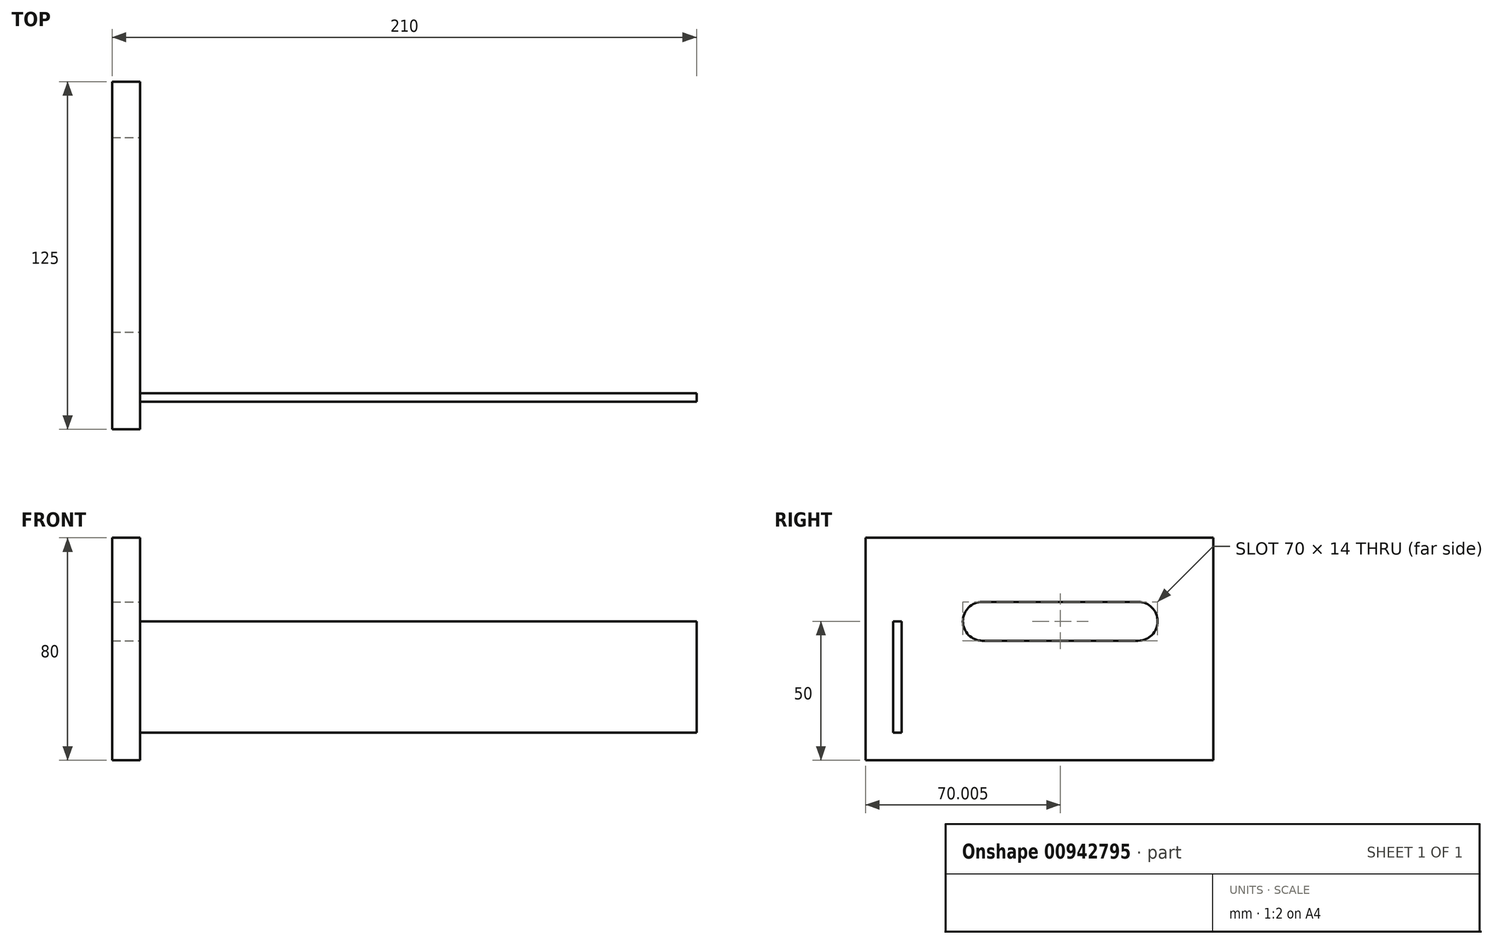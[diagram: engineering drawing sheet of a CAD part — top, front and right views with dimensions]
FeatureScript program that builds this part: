
annotation { "Feature Type Name" : "Feature", "Feature Type Description" : "" }
export const myFeature = defineFeature(function(context is Context, id is Id, definition is map)
    precondition{}
    {
        {
            var Q0;
            Q0=qCreatedBy(makeId("Top.planeOp"),FACE);
            var sketch = newSketch(context, id + "F0", { "sketchPlane" : qUnion([Q0])});
            skLineSegment(sketch, "E0.bottom", {"start": v(-39.22, -18.45) * mm, "end": v(-29.22, -18.45) * mm});
            skLineSegment(sketch, "E0.top", {"start": v(-39.22, 106.55) * mm, "end": v(-29.22, 106.55) * mm});
            skLineSegment(sketch, "E0.left", {"start": v(-39.22, -18.45) * mm, "end": v(-39.22, 106.55) * mm});
            skLineSegment(sketch, "E0.right", {"start": v(-29.22, -18.45) * mm, "end": v(-29.22, 106.55) * mm});
            skLineSegment(sketch, "E1.top", {"start": v(-29.22, -8.45) * mm, "end": v(-19.22, -8.45) * mm});
            skLineSegment(sketch, "E1.left", {"start": v(-29.22, -18.45) * mm, "end": v(-29.22, -8.45) * mm});
            skLineSegment(sketch, "E2.bottom", {"start": v(-29.22, -8.45) * mm, "end": v(295.78, -8.45) * mm});
            skLineSegment(sketch, "E2.top", {"start": v(-29.22, 31.55) * mm, "end": v(295.78, 31.55) * mm});
            skLineSegment(sketch, "E2.left", {"start": v(-29.22, -8.45) * mm, "end": v(-29.22, 31.55) * mm});
            skLineSegment(sketch, "E2.right", {"start": v(420.78, -8.45) * mm, "end": v(420.78, 31.55) * mm});
            skLineSegment(sketch, "E3.bottom", {"start": v(-29.22, -8.45) * mm, "end": v(170.78, -8.45) * mm});
            skLineSegment(sketch, "E3.top", {"start": v(-29.22, -5.45) * mm, "end": v(170.78, -5.45) * mm});
            skLineSegment(sketch, "E3.left", {"start": v(-29.22, -8.45) * mm, "end": v(-29.22, -5.45) * mm});
            skLineSegment(sketch, "E3.right", {"start": v(170.78, -8.45) * mm, "end": v(170.78, -5.45) * mm});
            skLineSegment(sketch, "E4", {"start": v(420.78, 11.55) * mm, "end": v(210.46, 11.55) * mm, "construction": true});
            skCircle(sketch, "E5", {"center": v(280.78, 11.55) * mm, "radius": 10 * mm});
            skCircle(sketch, "E6", {"center": v(360.78, 11.55) * mm, "radius": 10 * mm});
            skCircle(sketch, "E7", {"center": v(400.78, 11.55) * mm, "radius": 10 * mm});
            skLineSegment(sketch, "E8.trimOffspring", {"start": v(305.78, 31.55) * mm, "end": v(375.78, 31.55) * mm});
            skLineSegment(sketch, "E9.trimOffspring", {"start": v(385.78, 31.55) * mm, "end": v(420.78, 31.55) * mm});
            skLineSegment(sketch, "E10.trimOffspring", {"start": v(385.78, -8.45) * mm, "end": v(420.78, -8.45) * mm});
            skLineSegment(sketch, "E11.trimOffspring", {"start": v(305.78, -8.45) * mm, "end": v(375.78, -8.45) * mm});
            skLineSegment(sketch, "E12", {"start": v(300.78, 26.55) * mm, "end": v(300.78, -3.45) * mm, "construction": true});
            skLineSegment(sketch, "E13", {"start": v(380.78, 26.55) * mm, "end": v(380.78, -3.45) * mm, "construction": true});
            skLineSegment(sketch, "E14", {"start": v(295.78, 31.55) * mm, "end": v(300.78, 26.55) * mm});
            skLineSegment(sketch, "E15", {"start": v(305.78, 31.55) * mm, "end": v(300.78, 26.55) * mm});
            skLineSegment(sketch, "E16", {"start": v(295.78, -8.45) * mm, "end": v(300.78, -3.45) * mm});
            skLineSegment(sketch, "E17", {"start": v(300.78, -3.45) * mm, "end": v(305.78, -8.45) * mm});
            skLineSegment(sketch, "E18", {"start": v(375.78, -8.45) * mm, "end": v(380.78, -3.45) * mm});
            skLineSegment(sketch, "E19", {"start": v(380.78, -3.45) * mm, "end": v(385.78, -8.45) * mm});
            skLineSegment(sketch, "E20", {"start": v(375.78, 31.55) * mm, "end": v(380.78, 26.55) * mm});
            skLineSegment(sketch, "E21", {"start": v(380.78, 26.55) * mm, "end": v(385.78, 31.55) * mm});
            skSolve(sketch);
        }
        {
            var Q0;
            Q0=makeQuery(id+"F0.imprint","IMPRINT",FACE,{"disambiguationData":[TD([[makeQuery(id+"F0.imprint","IMPRINT",EDGE,{"derivedFrom":sQuery(id+"F0.wireOp",EDGE,"E0.bottom")}),1.0]])]});
            extrude(context, id + "F1", {"entities" : qUnion([Q0]), "depth" : 80 * mm, "offsetDistance" : 25 * mm});
        }
        {
            var Q0;
            Q0=makeQuery(id+"F0.imprint","IMPRINT",FACE,{"disambiguationData":[TD([[makeQuery(id+"F0.imprint","IMPRINT",EDGE,{"derivedFrom":sQuery(id+"F0.wireOp",EDGE,"E2.bottom")}),1.0]])]});
            extrude(context, id + "F2", {"entities" : qUnion([Q0]), "operationType" : NewBodyOperationType.ADD, "depth" : 13 * mm, "offsetDistance" : 25 * mm, "hasSecondDirection" : true, "secondDirectionOppositeDirection" : false, "secondDirectionDepth" : 10 * mm});
        }
        {
            var Q0;
            Q0=makeQuery(id+"F0.imprint","IMPRINT",FACE,{"disambiguationData":[TD([[makeQuery(id+"F0.imprint","IMPRINT",EDGE,{"derivedFrom":sQuery(id+"F0.wireOp",EDGE,"E3.top")}),-1.0]])]});
            extrude(context, id + "F3", {"entities" : qUnion([Q0]), "operationType" : NewBodyOperationType.ADD, "depth" : 50 * mm, "offsetDistance" : 25 * mm, "hasSecondDirection" : true, "secondDirectionOppositeDirection" : false, "secondDirectionDepth" : 10 * mm});
        }
        {
            var Q0;
            Q0=makeQuery(id+"F1.opExtrude","SWEPT_FACE",FACE,{"disambiguationData":[OSD([sQuery(id+"F0.wireOp",EDGE,"E0.right"),sQuery(id+"F0.wireOp",EDGE,"E1.left"),sQuery(id+"F0.wireOp",EDGE,"E2.left"),sQuery(id+"F0.wireOp",EDGE,"E3.left")])]});
            var sketch = newSketch(context, id + "F4", { "sketchPlane" : qUnion([Q0])});
            skLineSegment(sketch, "E22", {"start": v(106.55, 80) * mm, "end": v(-86.62, 80) * mm, "construction": true});
            skLineSegment(sketch, "E23", {"start": v(106.55, 0) * mm, "end": v(106.55, 117.68) * mm, "construction": true});
            skLineSegment(sketch, "E24.0", {"start": v(106.55, 50) * mm, "end": v(-86.62, 50) * mm, "construction": true});
            skLineSegment(sketch, "E25.0", {"start": v(79.55, 0) * mm, "end": v(79.55, 117.68) * mm, "construction": true});
            skLineSegment(sketch, "E26.0", {"start": v(23.55, 0) * mm, "end": v(23.55, 117.68) * mm, "construction": true});
            skCircle(sketch, "E27", {"center": v(23.55, 50) * mm, "radius": 7 * mm});
            skCircle(sketch, "E28", {"center": v(79.55, 50) * mm, "radius": 7 * mm});
            skLineSegment(sketch, "E29", {"start": v(23.55, 43) * mm, "end": v(79.55, 43) * mm});
            skPoint(sketch, "E29.startSnap0", {"position": v(23.55, 58.84) * mm});
            skLineSegment(sketch, "E30", {"start": v(23.55, 57) * mm, "end": v(79.55, 57) * mm});
            skSolve(sketch);
        }
        {
            var Q0;
            {var subQ0=sQuery(id+"F4.wireOp",EDGE,"E29");Q0=makeQuery(id+"F4.imprint","IMPRINT",FACE,{"disambiguationData":[TD([[makeQuery(id+"F4.imprint","IMPRINT",EDGE,{"derivedFrom":subQ0}),1.0]])]});}
            var Q1;
            {var subQ0=sQuery(id+"F4.wireOp",EDGE,"E27");var subQ1=makeQuery(id+"F4.imprint","INTERSECT",VERTEX,{"derivedFrom":[subQ0,sQuery(id+"F4.wireOp",EDGE,"E29")]});Q1=makeQuery(id+"F4.imprint","IMPRINT",FACE,{"disambiguationData":[TD([[makeQuery(id+"F4.imprint","IMPRINT",EDGE,{"disambiguationData":[TD([[subQ1,1.0]])],"derivedFrom":subQ0}),1.0]])]});}
            var Q2;
            {var subQ0=sQuery(id+"F4.wireOp",EDGE,"E28");var subQ1=makeQuery(id+"F4.imprint","INTERSECT",VERTEX,{"derivedFrom":[subQ0,sQuery(id+"F4.wireOp",EDGE,"E29")]});Q2=makeQuery(id+"F4.imprint","IMPRINT",FACE,{"disambiguationData":[TD([[makeQuery(id+"F4.imprint","IMPRINT",EDGE,{"disambiguationData":[TD([[subQ1,1.0]])],"derivedFrom":subQ0}),1.0]])]});}
            extrude(context, id + "F5", {"entities" : qUnion([Q0, Q1, Q2]), "operationType" : NewBodyOperationType.REMOVE, "oppositeDirection" : true, "depth" : 25 * mm, "offsetDistance" : 25 * mm});
        }
    });
